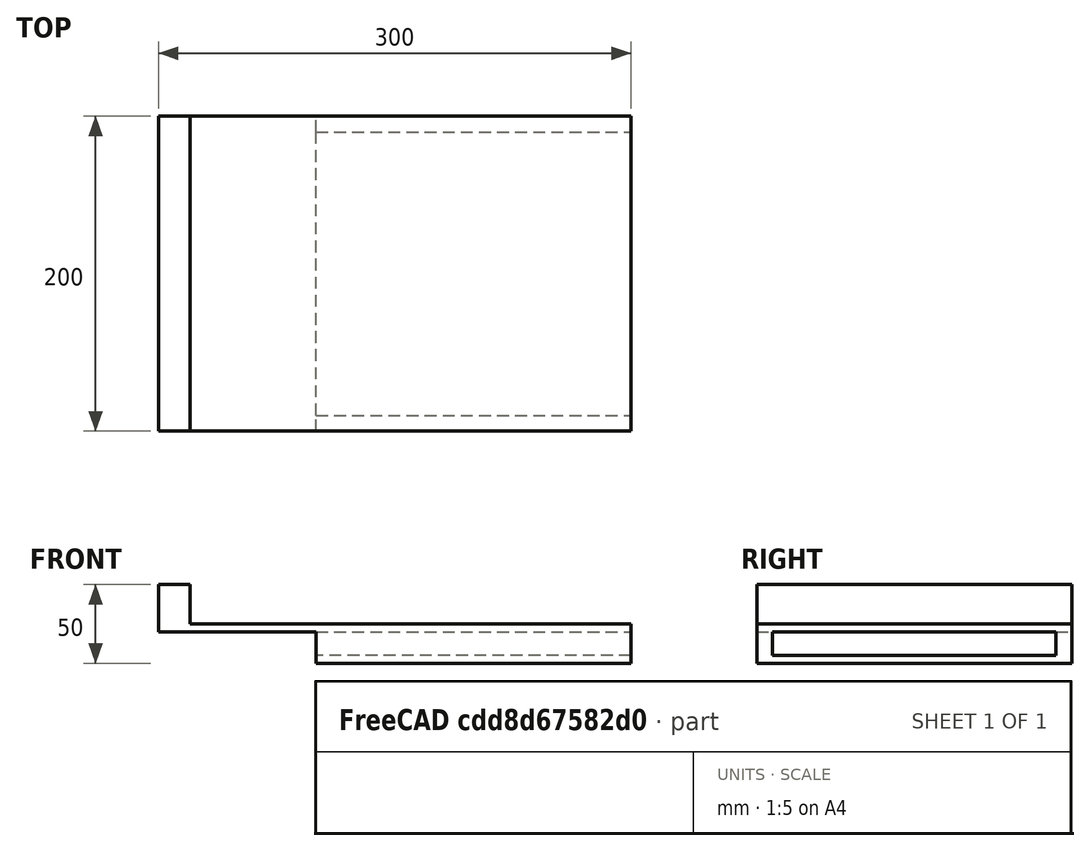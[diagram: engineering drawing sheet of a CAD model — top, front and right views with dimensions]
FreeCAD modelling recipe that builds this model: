
FCSTD DOCUMENT  (FreeCAD 0.19R24367 (Git))
Label: Letterbox Device
License: All rights reserved
LicenseURL: http://en.wikipedia.org/wiki/All_rights_reserved
objects: Part::Box×5, Part::MultiFuse×1
note: 6 computed .brp shape members not serialized (recipe doc carries the construction recipe); baked Part::Feature solids carry a one-line shape summary decoded from their .brp

FEATURE [Part::Box] Box  label="Cube"
  AttacherType = Attacher::AttachEngine3D
  Height = 5
  Length = 200
  Placement = pos=(100,0,-20) rot=(0,0,1;0rad)
  Width = 200
FEATURE [Part::Box] Box001  label="Cube001"
  AttacherType = Attacher::AttachEngine3D
  Height = 30
  Length = 20
  Width = 200
FEATURE [Part::Box] Box002  label="Cube002"
  AttacherType = Attacher::AttachEngine3D
  Height = 20
  Length = 200
  Placement = pos=(100,190,-20) rot=(0,0,1;0rad)
  Width = 10
FEATURE [Part::Box] Box003  label="Cube003"
  AttacherType = Attacher::AttachEngine3D
  Height = 20
  Length = 200
  Placement = pos=(100,0,-20) rot=(0,0,1;0rad)
  Width = 10
FEATURE [Part::Box] Box004  label="Cube004"
  AttacherType = Attacher::AttachEngine3D
  Height = 5
  Length = 300
  Width = 200
FEATURE [Part::MultiFuse] Fusion
  Shapes = -> [Box,Box001,Box002,Box003,Box004]
